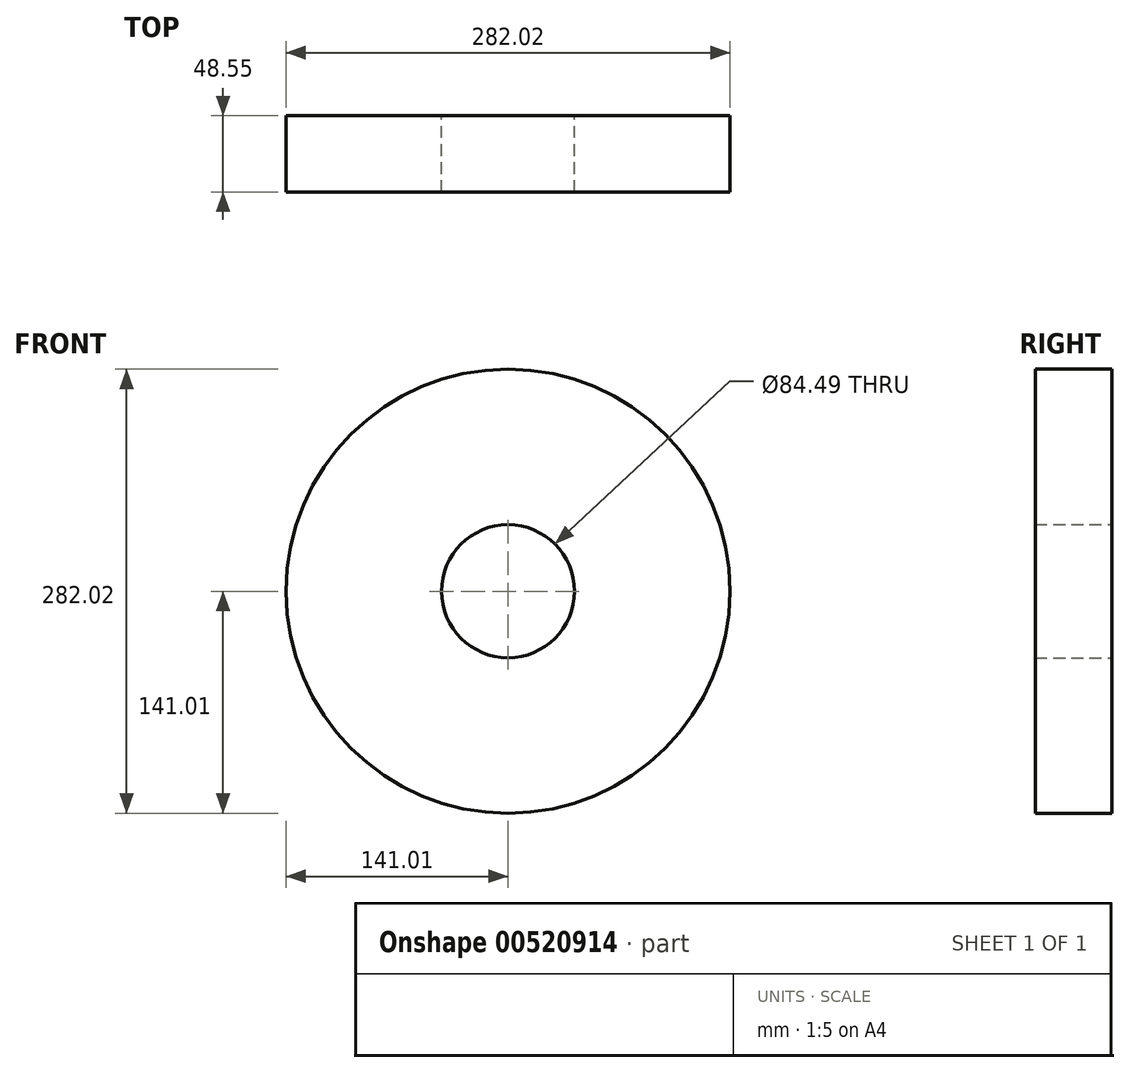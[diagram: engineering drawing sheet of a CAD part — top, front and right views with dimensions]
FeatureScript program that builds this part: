
annotation { "Feature Type Name" : "Feature", "Feature Type Description" : "" }
export const myFeature = defineFeature(function(context is Context, id is Id, definition is map)
    precondition{}
    {
        {
            var Q0;
            Q0=qCreatedBy(makeId("Top.planeOp"),FACE);
            var sketch = newSketch(context, id + "F0", { "sketchPlane" : qUnion([Q0])});
            skLineSegment(sketch, "E0.bottom", {"start": v(-141.01, 0) * mm, "end": v(-42.24, 0) * mm});
            skLineSegment(sketch, "E0.top", {"start": v(-141.01, -48.55) * mm, "end": v(-42.24, -48.55) * mm});
            skLineSegment(sketch, "E0.left", {"start": v(-141.01, 0) * mm, "end": v(-141.01, -48.55) * mm});
            skLineSegment(sketch, "E0.right", {"start": v(-42.24, 0) * mm, "end": v(-42.24, -48.55) * mm});
            skLineSegment(sketch, "E1", {"start": v(0, 50.48) * mm, "end": v(0, -70.75) * mm});
            skSolve(sketch);
        }
        {
            var Q0;
            Q0=makeQuery(id+"F0.imprint","IMPRINT",FACE,{"disambiguationData":[TD([[makeQuery(id+"F0.imprint","IMPRINT",EDGE,{"derivedFrom":sQuery(id+"F0.wireOp",EDGE,"E0.bottom")}),-1.0]])]});
            var Q1;
            Q1=sQuery(id+"F0.wireOp",EDGE,"E1");
            revolve(context, id + "F1", {"entities" : qUnion([Q0]), "axis" : qUnion([Q1]), "revolveType" : RevolveType.FULL});
        }
    });
